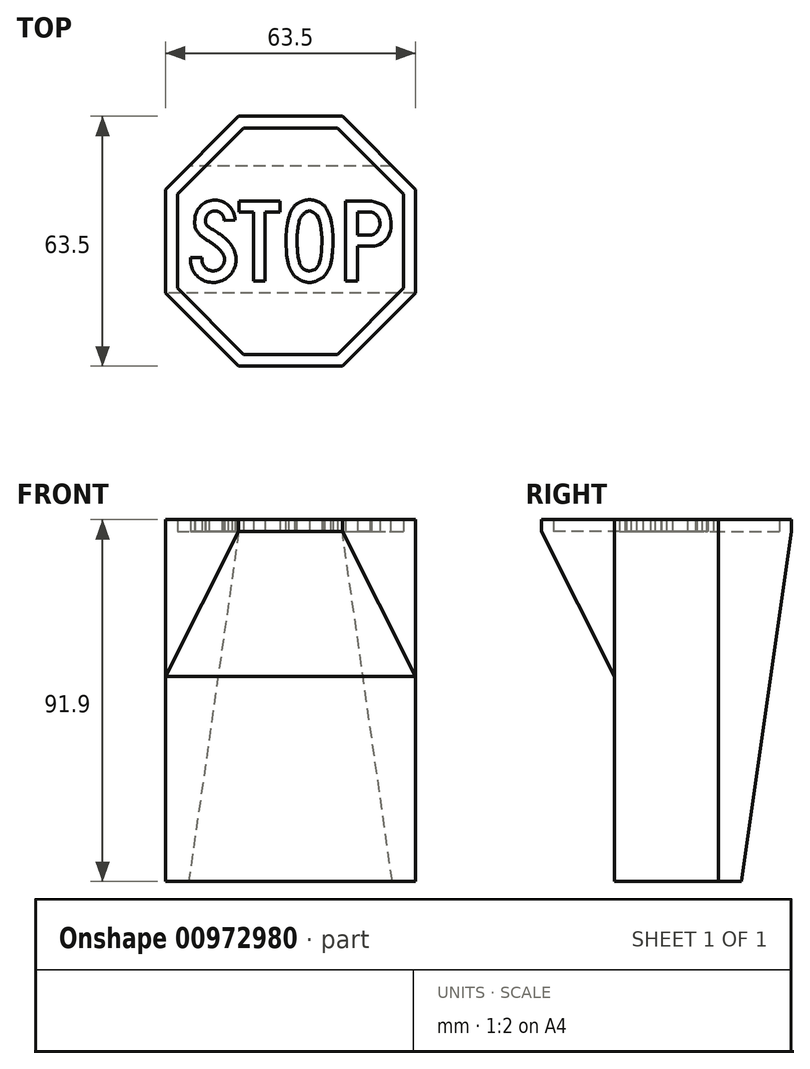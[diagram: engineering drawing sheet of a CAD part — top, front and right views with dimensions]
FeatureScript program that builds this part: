
annotation { "Feature Type Name" : "Feature", "Feature Type Description" : "" }
export const myFeature = defineFeature(function(context is Context, id is Id, definition is map)
    precondition{}
    {
        {
            var Q0;
            Q0=qCreatedBy(makeId("Top.planeOp"),FACE);
            var sketch = newSketch(context, id + "F0", { "sketchPlane" : qUnion([Q0])});
            skCircle(sketch, "E0.cCircle", {"center": v(0, 0) * mm, "radius": 34.37 * mm, "construction": true});
            skLineSegment(sketch, "E0.0", {"start": v(-13.15, 31.75) * mm, "end": v(13.15, 31.75) * mm});
            skLineSegment(sketch, "E0.1", {"start": v(13.15, 31.75) * mm, "end": v(31.75, 13.15) * mm});
            skLineSegment(sketch, "E0.2", {"start": v(31.75, 13.15) * mm, "end": v(31.75, -13.15) * mm});
            skLineSegment(sketch, "E0.3", {"start": v(31.75, -13.15) * mm, "end": v(13.15, -31.75) * mm});
            skLineSegment(sketch, "E0.4", {"start": v(13.15, -31.75) * mm, "end": v(-13.15, -31.75) * mm});
            skLineSegment(sketch, "E0.5", {"start": v(-13.15, -31.75) * mm, "end": v(-31.75, -13.15) * mm});
            skLineSegment(sketch, "E0.6", {"start": v(-31.75, -13.15) * mm, "end": v(-31.75, 13.15) * mm});
            skLineSegment(sketch, "E0.7", {"start": v(-31.75, 13.15) * mm, "end": v(-13.15, 31.75) * mm});
            skSolve(sketch);
        }
        {
            var Q0;
            Q0 = qSketchRegion(id + "F0", true);
            extrude(context, id + "F1", {"entities" : qUnion([Q0]), "oppositeDirection" : true, "depth" : 88.9 * mm, "offsetDistance" : 25.4 * mm});
        }
        {
            var Q0;
            Q0=makeQuery(id+"F1.opExtrude","SWEPT_FACE",FACE,{"disambiguationData":[OSD([sQuery(id+"F0.wireOp",EDGE,"E0.6")])]});
            var sketch = newSketch(context, id + "F2", { "sketchPlane" : qUnion([Q0])});
            skLineSegment(sketch, "E1", {"start": v(0, 0) * mm, "end": v(-31.75, 0) * mm});
            skLineSegment(sketch, "E2.MirrorCS", {"start": v(0, 0) * mm, "end": v(31.75, 0) * mm});
            skLineSegment(sketch, "E3", {"start": v(31.75, 0) * mm, "end": v(31.75, -88.9) * mm});
            skLineSegment(sketch, "E4", {"start": v(14.66, -88.9) * mm, "end": v(-31.75, -88.9) * mm});
            skLineSegment(sketch, "E5", {"start": v(-31.75, -88.9) * mm, "end": v(-31.75, 0) * mm});
            skLineSegment(sketch, "E6", {"start": v(14.66, -88.9) * mm, "end": v(8.31, -88.9) * mm});
            skPoint(sketch, "E7.orphan", {"position": v(21.01, -88.9) * mm});
            skLineSegment(sketch, "E8", {"start": v(13.15, -88.9) * mm, "end": v(31.75, -88.9) * mm});
            skLineSegment(sketch, "E9", {"start": v(0, -88.9) * mm, "end": v(-6.35, -88.9) * mm});
            skLineSegment(sketch, "E10", {"start": v(-6.35, -88.9) * mm, "end": v(-12.7, -88.9) * mm});
            skLineSegment(sketch, "E11", {"start": v(-12.7, -88.9) * mm, "end": v(-19.05, -88.9) * mm});
            skLineSegment(sketch, "E12", {"start": v(-13.15, -88.9) * mm, "end": v(31.75, 0) * mm});
            skLineSegment(sketch, "E13", {"start": v(-19.05, -88.9) * mm, "end": v(-31.75, 0) * mm});
            skSolve(sketch);
        }
        {
            var Q0;
            {var subQ0=sQuery(id+"F2.wireOp",EDGE,"E5");Q0=makeQuery(id+"F2.imprint","IMPRINT",FACE,{"disambiguationData":[TD([[makeQuery(id+"F2.imprint","IMPRINT",EDGE,{"derivedFrom":subQ0}),-1.0]])]});}
            var Q1;
            {var subQ0=sQuery(id+"F2.wireOp",EDGE,"jV5SaWTU-9QsE-opv1-VP0P-y0ptpn6lwSnb");var subQ1=sQuery(id+"F0.wireOp",EDGE,"E0.6");var subQ2=makeQuery(id+"F1.opExtrude","SWEPT_EDGE",EDGE,{"disambiguationData":[OSD([sQuery(id+"F0.wireOp",EDGE,"E0.5"),subQ1])]});var subQ3=makeQuery(id+"F2.imprint","INTERSECT",VERTEX,{"derivedFrom":[subQ2,subQ0]});Q1=makeQuery(id+"F2.imprint","IMPRINT",FACE,{"disambiguationData":[TD([[makeQuery(id+"F2.imprint","IMPRINT",EDGE,{"disambiguationData":[TD([[subQ3,-1.0]])],"derivedFrom":subQ0}),1.0]])]});}
            var Q2;
            {var subQ0=sQuery(id+"F2.wireOp",EDGE,"E4");var subQ1=sQuery(id+"F2.wireOp",EDGE,"jV5SaWTU-9QsE-opv1-VP0P-y0ptpn6lwSnb");var subQ2=makeQuery(id+"F2.imprint","INTERSECT",VERTEX,{"derivedFrom":[sQuery(id+"F2.wireOp",EDGE,"heyR2Hmy-5QPG-FOdl-Z93e-mRFAagvmiP7r"),subQ1,subQ0]});Q2=makeQuery(id+"F2.imprint","IMPRINT",FACE,{"disambiguationData":[TD([[makeQuery(id+"F2.imprint","IMPRINT",EDGE,{"disambiguationData":[TD([[subQ2,-1.0]])],"derivedFrom":subQ1}),1.0]])]});}
            var Q3;
            {var subQ4=sQuery(id+"F2.wireOp",EDGE,"JUMX4e05-irpo-ZofT-aYDr-bJa91oU9Ee8P");var subQ6=sQuery(id+"F2.wireOp",EDGE,"AKcFHBRH-ovDV-q2iI-lgTK-DhJX03LWiosI");var subQ7=makeQuery(id+"F2.imprint","INTERSECT",VERTEX,{"derivedFrom":[subQ4,subQ6]});Q3=makeQuery(id+"F2.imprint","IMPRINT",FACE,{"disambiguationData":[TD([[makeQuery(id+"F2.imprint","IMPRINT",EDGE,{"disambiguationData":[TD([[subQ7,1.0]])],"derivedFrom":subQ4}),1.0]])]});}
            var Q4;
            {var subQ0=sQuery(id+"F2.wireOp",EDGE,"E4");var subQ1=makeQuery(id+"F1.opExtrude","SWEPT_EDGE",EDGE,{"disambiguationData":[OSD([sQuery(id+"F0.wireOp",EDGE,"E0.5"),sQuery(id+"F0.wireOp",EDGE,"E0.6")])]});var subQ2=makeQuery(id+"F2.imprint","INTERSECT",VERTEX,{"derivedFrom":[subQ1,subQ0]});Q4=makeQuery(id+"F2.imprint","IMPRINT",FACE,{"disambiguationData":[TD([[makeQuery(id+"F2.imprint","IMPRINT",EDGE,{"disambiguationData":[TD([[subQ2,1.0]])],"derivedFrom":subQ0}),-1.0]])]});}
            var Q5;
            Q5=makeQuery(id+"F1.opExtrude","SWEPT_FACE",FACE,{"disambiguationData":[OSD([sQuery(id+"F0.wireOp",EDGE,"E0.3")])]});
            var Q6;
            {var subQ0=sQuery(id+"F2.wireOp",EDGE,"E3");Q6=makeQuery(id+"F2.imprint","IMPRINT",FACE,{"disambiguationData":[TD([[makeQuery(id+"F2.imprint","IMPRINT",EDGE,{"derivedFrom":subQ0}),-1.0]])]});}
            var Q7;
            {var subQ0=sQuery(id+"F2.wireOp",EDGE,"VHKm9X3M-lhd3-aAJ8-6689-DRtZFMRUWEL7");var subQ1=sQuery(id+"F0.wireOp",EDGE,"E0.6");var subQ2=makeQuery(id+"F1.opExtrude","CAP_EDGE",EDGE,{"disambiguationData":[OSD([subQ1])],"isStart":false});var subQ3=makeQuery(id+"F2.imprint","INTERSECT",VERTEX,{"derivedFrom":[subQ2,sQuery(id+"F2.wireOp",EDGE,"E6"),subQ0]});Q7=makeQuery(id+"F2.imprint","IMPRINT",FACE,{"disambiguationData":[TD([[makeQuery(id+"F2.imprint","IMPRINT",EDGE,{"disambiguationData":[TD([[subQ3,-1.0]])],"derivedFrom":subQ0}),-1.0]])]});}
            var Q8;
            {var subQ4=sQuery(id+"F2.wireOp",EDGE,"E6");Q8=makeQuery(id+"F2.imprint","IMPRINT",FACE,{"disambiguationData":[TD([[makeQuery(id+"F2.imprint","IMPRINT",EDGE,{"derivedFrom":subQ4}),-1.0]])]});}
            var Q9;
            Q9=makeQuery(id+"F1.opExtrude","SWEPT_FACE",FACE,{"disambiguationData":[OSD([sQuery(id+"F0.wireOp",EDGE,"E0.2")])]});
            extrude(context, id + "F3", {"entities" : qUnion([Q0, Q1, Q2, Q3, Q4, Q5, Q6, Q7, Q8]), "operationType" : NewBodyOperationType.REMOVE, "endBound" : BoundingType.UP_TO_SURFACE, "oppositeDirection" : true, "depth" : 25.4 * mm, "endBoundEntityFace" : qUnion([Q9]), "offsetDistance" : 25.4 * mm});
        }
        {
            var Q0;
            Q0=makeQuery(id+"F1.opExtrude","CAP_FACE",FACE,{"disambiguationData":[OSD([sQuery(id+"F0.wireOp",EDGE,"E0.0"),sQuery(id+"F0.wireOp",EDGE,"E0.1"),sQuery(id+"F0.wireOp",EDGE,"E0.2"),sQuery(id+"F0.wireOp",EDGE,"E0.3"),sQuery(id+"F0.wireOp",EDGE,"E0.4"),sQuery(id+"F0.wireOp",EDGE,"E0.5"),sQuery(id+"F0.wireOp",EDGE,"E0.6"),sQuery(id+"F0.wireOp",EDGE,"E0.7")])],"isStart":true});
            var sketch = newSketch(context, id + "F4", { "sketchPlane" : qUnion([Q0])});
            skLineSegment(sketch, "E14.0", {"start": v(-28.75, 11.9) * mm, "end": v(-11.9, 28.75) * mm});
            skLineSegment(sketch, "E14.1", {"start": v(-28.75, -11.9) * mm, "end": v(-28.75, 11.9) * mm});
            skLineSegment(sketch, "E14.2", {"start": v(-11.9, 28.75) * mm, "end": v(11.9, 28.75) * mm});
            skLineSegment(sketch, "E14.3", {"start": v(-11.9, -28.75) * mm, "end": v(-28.75, -11.9) * mm});
            skLineSegment(sketch, "E14.4", {"start": v(11.9, 28.75) * mm, "end": v(28.75, 11.9) * mm});
            skLineSegment(sketch, "E14.5", {"start": v(28.75, 11.9) * mm, "end": v(28.75, -11.9) * mm});
            skLineSegment(sketch, "E14.6", {"start": v(28.75, -11.9) * mm, "end": v(11.9, -28.75) * mm});
            skLineSegment(sketch, "E14.7", {"start": v(11.9, -28.75) * mm, "end": v(-11.9, -28.75) * mm});
            skLineSegment(sketch, "E15.bottom", {"start": v(28.75, -11.9) * mm, "end": v(-28.75, -11.9) * mm});
            skLineSegment(sketch, "E15.top", {"start": v(28.75, 11.9) * mm, "end": v(-28.75, 11.9) * mm});
            skLineSegment(sketch, "E15.left", {"start": v(28.75, -11.9) * mm, "end": v(28.75, 11.9) * mm});
            skPoint(sketch, "E15.middle", {"position": v(0, 0) * mm});
            skLineSegment(sketch, "E16.bottom", {"start": v(33.9, 33.9) * mm, "end": v(-33.9, 33.9) * mm});
            skLineSegment(sketch, "E16.top", {"start": v(33.9, -33.9) * mm, "end": v(-33.9, -33.9) * mm});
            skLineSegment(sketch, "E16.left", {"start": v(33.9, 33.9) * mm, "end": v(33.9, -33.9) * mm});
            skLineSegment(sketch, "E16.right", {"start": v(-33.9, 33.9) * mm, "end": v(-33.9, -33.9) * mm});
            skLineSegment(sketch, "E17", {"start": v(-28.75, -10.78) * mm, "end": v(28.75, -10.78) * mm});
            skLineSegment(sketch, "E18.MirrorCS", {"start": v(-28.75, 10.78) * mm, "end": v(28.75, 10.78) * mm});
            skPoint(sketch, "E19", {"position": v(-22.45, -4.1) * mm});
            skPoint(sketch, "E20", {"position": v(-25.43, -4.1) * mm});
            skPoint(sketch, "E21", {"position": v(-16.83, -4.1) * mm});
            skPoint(sketch, "E22", {"position": v(-20.76, 0) * mm});
            skPoint(sketch, "E23", {"position": v(-20.76, -7.34) * mm});
            skArc(sketch, "E24", {"start": v(-22.45, -4.1) * mm, "mid": v(-18.95, -7.48) * mm, "end": v(-17.44, -2.86) * mm});
            skFitSpline(sketch, "E25", {"points": [v(-20.76, 0) * mm, v(-17.8, -2.36) * mm, v(-16.83, -4.1) * mm], "startDerivative": vector(5.92, -4.06) * mm, "endDerivative": vector(1.7, -4.16) * mm});
            skLineSegment(sketch, "E26", {"start": v(-22.45, -4.1) * mm, "end": v(-25.43, -4.1) * mm});
            skArc(sketch, "E27", {"start": v(-25.43, -4.1) * mm, "mid": v(-18.16, -10.32) * mm, "end": v(-14.9, -1.33) * mm});
            skFitSpline(sketch, "E28", {"points": [v(-15.87, 0) * mm, v(-14.9, -1.33) * mm], "startDerivative": vector(1.2, -1.18) * mm, "endDerivative": vector(0.57, -1.44) * mm});
            skPoint(sketch, "E29.trimOffspring.end.orphan", {"position": v(-27.32, 0) * mm});
            skPoint(sketch, "E30", {"position": v(-16.86, 5.28) * mm});
            skPoint(sketch, "E31", {"position": v(-14.12, 5.32) * mm});
            skPoint(sketch, "E32", {"position": v(-21.58, 5.28) * mm});
            skPoint(sketch, "E33", {"position": v(-19.24, 7.66) * mm});
            skArc(sketch, "E34", {"start": v(-16.86, 5.28) * mm, "mid": v(-19.22, 7.66) * mm, "end": v(-21.58, 5.28) * mm});
            skFitSpline(sketch, "E35", {"points": [v(-21.58, 5.28) * mm, v(-21.4, 4.17) * mm, v(-18.58, 2.21) * mm, v(-15.87, 0) * mm], "startDerivative": vector(-0.47, -5.02) * mm, "endDerivative": vector(6.25, -5.82) * mm});
            skArc(sketch, "E36", {"start": v(-14.12, 5.32) * mm, "mid": v(-19.23, 10.4) * mm, "end": v(-24.32, 5.3) * mm});
            skFitSpline(sketch, "E37", {"points": [v(-24.32, 5.3) * mm, v(-24.22, 3.6) * mm, v(-22.95, 1.57) * mm, v(-20.76, 0) * mm], "startDerivative": vector(-0.33, -5.74) * mm, "endDerivative": vector(6.39, -3.84) * mm});
            skLineSegment(sketch, "E38", {"start": v(-16.86, 5.28) * mm, "end": v(-14.12, 5.32) * mm});
            skPoint(sketch, "E39.start.orphan", {"position": v(-12.29, 0) * mm});
            skLineSegment(sketch, "E40.bottom", {"start": v(-9.37, -10.14) * mm, "end": v(-6.43, -10.14) * mm});
            skLineSegment(sketch, "E40.top", {"start": v(-9.37, 10.14) * mm, "end": v(-6.43, 10.14) * mm});
            skLineSegment(sketch, "E40.left", {"start": v(-9.37, -10.14) * mm, "end": v(-9.37, 7.43) * mm});
            skLineSegment(sketch, "E40.right", {"start": v(-6.43, -10.14) * mm, "end": v(-6.43, 7.43) * mm});
            skLineSegment(sketch, "E41.top", {"start": v(-2.65, 7.43) * mm, "end": v(-6.43, 7.43) * mm});
            skLineSegment(sketch, "E41.left", {"start": v(-2.65, 10.14) * mm, "end": v(-2.65, 7.43) * mm});
            skLineSegment(sketch, "E41.right", {"start": v(-13.03, 10.14) * mm, "end": v(-13.03, 7.43) * mm});
            skLineSegment(sketch, "E42", {"start": v(-9.37, 10.14) * mm, "end": v(-13.03, 10.14) * mm});
            skLineSegment(sketch, "E43", {"start": v(-6.43, 10.14) * mm, "end": v(-2.65, 10.14) * mm});
            skPoint(sketch, "E44.orphan", {"position": v(-13.03, 10.32) * mm});
            skLineSegment(sketch, "E45.trimOffspring", {"start": v(-9.37, 7.43) * mm, "end": v(-13.03, 7.43) * mm});
            skLineSegment(sketch, "E46", {"start": v(13.96, 10.14) * mm, "end": v(13.96, -10.14) * mm});
            skLineSegment(sketch, "E47", {"start": v(13.96, -10.14) * mm, "end": v(16.98, -10.14) * mm});
            skLineSegment(sketch, "E48", {"start": v(16.98, -10.14) * mm, "end": v(16.98, -1.27) * mm});
            skLineSegment(sketch, "E49", {"start": v(13.96, 10.14) * mm, "end": v(20.6, 10.14) * mm});
            skLineSegment(sketch, "E50", {"start": v(16.98, 1.51) * mm, "end": v(16.98, 7.43) * mm});
            skLineSegment(sketch, "E51", {"start": v(16.98, 7.43) * mm, "end": v(20.22, 7.43) * mm});
            skLineSegment(sketch, "E52", {"start": v(20.22, 1.51) * mm, "end": v(16.98, 1.51) * mm});
            skFitSpline(sketch, "E53", {"points": [v(20.22, 7.43) * mm, v(22.37, 5.9) * mm, v(22.43, 3.23) * mm, v(20.22, 1.51) * mm], "startDerivative": vector(8.54, -0.14) * mm, "endDerivative": vector(-8.25, 0.77) * mm});
            skLineSegment(sketch, "E54", {"start": v(16.98, -1.27) * mm, "end": v(20.6, -1.27) * mm});
            skPoint(sketch, "E55", {"position": v(4.8, 10.54) * mm});
            skLineSegment(sketch, "E56", {"start": v(0, 0) * mm, "end": v(4.8, 0) * mm});
            skPoint(sketch, "E57.MirrorP", {"position": v(4.8, -10.54) * mm});
            skFitSpline(sketch, "E58", {"points": [v(4.8, 10.54) * mm, v(1.72, 9.54) * mm, v(-0.36, 6.48) * mm, v(-0.9, -4.8) * mm, v(1.95, -9.7) * mm, v(4.8, -10.54) * mm, v(8.77, -8.69) * mm, v(10.48, -4.31) * mm, v(10.4, 4.6) * mm, v(8.01, 9.55) * mm, v(4.8, 10.54) * mm]});
            skLineSegment(sketch, "E59", {"start": v(4.8, 0) * mm, "end": v(4.8, 2.13) * mm});
            skFitSpline(sketch, "E60.MirrorCS", {"points": [v(4.8, 10.54) * mm, v(7.9, 9.54) * mm, v(9.97, 6.48) * mm, v(10.5, -4.8) * mm, v(7.66, -9.7) * mm, v(4.8, -10.54) * mm, v(0.84, -8.69) * mm, v(-0.87, -4.31) * mm, v(-0.78, 4.6) * mm, v(1.6, 9.55) * mm, v(4.8, 10.54) * mm]});
            skPoint(sketch, "E61", {"position": v(4.8, 7.79) * mm});
            skPoint(sketch, "E62", {"position": v(4.8, -7.62) * mm});
            skFitSpline(sketch, "E63", {"points": [v(4.8, 7.79) * mm, v(2.55, 5.95) * mm, v(1.84, -3.12) * mm, v(3.07, -6.9) * mm, v(4.8, -7.62) * mm], "startDerivative": vector(-12.15, -5.2) * mm, "endDerivative": vector(11.19, -2.47) * mm});
            skFitSpline(sketch, "E64.MirrorCS", {"points": [v(4.8, 7.79) * mm, v(7.07, 5.95) * mm, v(7.77, -3.12) * mm, v(6.54, -6.9) * mm, v(4.8, -7.62) * mm], "startDerivative": vector(12.15, -5.2) * mm, "endDerivative": vector(-11.19, -2.47) * mm});
            skFitSpline(sketch, "E65", {"points": [v(20.6, 10.14) * mm, v(23.97, 8.83) * mm, v(25.32, 6.13) * mm, v(25.42, 2.7) * mm, v(23.87, 0) * mm, v(21.38, -1.27) * mm, v(20.6, -1.27) * mm], "startDerivative": vector(19.7, -4.63) * mm, "endDerivative": vector(-7.28, 1.07) * mm});
            skLineSegment(sketch, "E66", {"start": v(-13.15, 31.75) * mm, "end": v(13.15, 31.75) * mm});
            skLineSegment(sketch, "E67", {"start": v(13.15, 31.75) * mm, "end": v(31.75, 13.15) * mm});
            skLineSegment(sketch, "E68", {"start": v(31.75, 13.15) * mm, "end": v(31.75, -13.15) * mm});
            skLineSegment(sketch, "E69", {"start": v(31.75, -13.15) * mm, "end": v(13.15, -31.75) * mm});
            skLineSegment(sketch, "E70", {"start": v(13.15, -31.75) * mm, "end": v(-13.15, -31.75) * mm});
            skLineSegment(sketch, "E71", {"start": v(-13.15, -31.75) * mm, "end": v(-31.75, -13.15) * mm});
            skLineSegment(sketch, "E72", {"start": v(-31.75, -13.15) * mm, "end": v(-31.75, 13.15) * mm});
            skLineSegment(sketch, "E73", {"start": v(-31.75, 13.15) * mm, "end": v(-13.15, 31.75) * mm});
            skSolve(sketch);
        }
        {
            var Q0;
            {var subQ12=sQuery(id+"F4.wireOp",EDGE,"E14.0");Q0=makeQuery(id+"F4.imprint","IMPRINT",FACE,{"disambiguationData":[TD([[makeQuery(id+"F4.imprint","IMPRINT",EDGE,{"derivedFrom":subQ12}),1.0]])]});}
            var Q1;
            Q1=makeQuery(id+"F4.imprint","IMPRINT",FACE,{"disambiguationData":[TD([[makeQuery(id+"F4.imprint","IMPRINT",EDGE,{"derivedFrom":sQuery(id+"F4.wireOp",EDGE,"E24")}),-1.0]])]});
            var Q2;
            Q2=makeQuery(id+"F4.imprint","IMPRINT",FACE,{"disambiguationData":[TD([[makeQuery(id+"F4.imprint","IMPRINT",EDGE,{"derivedFrom":sQuery(id+"F4.wireOp",EDGE,"E40.bottom")}),1.0]])]});
            var Q3;
            Q3=makeQuery(id+"F4.imprint","IMPRINT",FACE,{"disambiguationData":[TD([[makeQuery(id+"F4.imprint","IMPRINT",EDGE,{"derivedFrom":sQuery(id+"F4.wireOp",EDGE,"E58")}),1.0]])]});
            var Q4;
            Q4=makeQuery(id+"F4.imprint","IMPRINT",FACE,{"disambiguationData":[TD([[makeQuery(id+"F4.imprint","IMPRINT",EDGE,{"derivedFrom":sQuery(id+"F4.wireOp",EDGE,"E46")}),1.0]])]});
            extrude(context, id + "F5", {"entities" : qUnion([Q0, Q1, Q2, Q3, Q4]), "operationType" : NewBodyOperationType.ADD, "depth" : 3 * mm, "offsetDistance" : 25.4 * mm});
        }
    });
